# Revit family: Hager-Univers-IP65-D300-H550-Cl.II-encl-CH-fr
name_source: partatom
category: Equipement électrique
units: mm (PartAtom-declared; Revit-internal decimal feet)

## family parameters
Configuration du panneau = Deux colonnes, circuits au sein
Cote de connecteur circulaire = Utiliser le diamètre
Couper avec des vides une fois chargée = Non
Hôte = Face
Partagée = Non
Point de calcul de pièce = Non
Type d'élément = Tableau de raccordement

## types (6) — shared parameters
Commentaires du type = Univers
EF000003 - mode de pose = EV000384 - saillie
EF000007 - couleur = EV000270 - gris
EF000040 - hauteur = 550 mm
EF000049 - profondeur = 300 mm  [stored 0.984252 ft]
EF000116 - numéro RAL = 7035
EF000118 - avec cadre/support de montage = Non
EF000266 - nombre de rangées = 3
EF001088 - possibilité de montage en saillie = Non
EF001131 - profondeur intérieure = 150 mm  [stored 0.492126 ft]
EF001596 - matériau du boîtier/corps = EV000139 - plastique
EF001613 - maintien de fonction = EV000494 - sans
EF003532 - convient pour utilisation à l’extérieur = Oui
EF004293 - indice de protection contre les chocs (IK) = EV008784 - IK10
EF004464 - type de porte = EV002646 - unique
EF005474 - indice de protection (IP) = EV006421 - IP65
EF006244 - couvercle/porte transparent(e) = Non
EF006306 - avec serrure = Oui
EF007800 - adapté à un parafoudre = Oui
EF009170 - épaisseur de matériau du boîtier = 2 mm  [stored 0.00656168 ft]
EF009171 - épaisseur de matériau de la porte/du couvercle = 2 mm  [stored 0.00656168 ft]
EF009212 - finition du couvercle = EV000116 - fermé
EF015940 - couvercle avec décharge de pression = Non
Fabricant = Hager
HG000002 - avec porte = Oui
HG000003 - Gamme = Univers
HG000006 - Encastré = Non
HG000009 - Porte à double battant = Non
HG000010 - Portes asymétriques = Non
HG000023 - Armoire double section = Non
HG000024 - Hauteur de la section basse = 800 mm
HG000026 - Installation au sol = Non
zero-valued in all types: EF000218 - profondeur d'encastrement, EF000437 - nombre d'entrées de conduit, EF009554 - nombre d'ouvertures pour plaques à bride, Elévation par défaut, HG000027 - Hauteur du socle

## per-type parameters (varying)
| type | EF000008 - largeur | EF000339 - type de capot | EF002950 - largeur en nombre de modules | EF004427 - nombre de modules | EF008873 - courant nominal (In) | HG000004 - Référence fabricant |
| saillie IP65 L1100 H550 P300  - FL34S | 1100 mm | EV001012 - couvercle | 48 | 144 | 630 A | FL34S |
| saillie IP65 L1100 H550 P300  - FL34SP | 1100 mm | EV001012 - couvercle | 48 | 144 | 630 A | FL34SP |
| saillie IP65 L600 H550 P300  - FL32S | 600 mm | EV004216 - porte | 24 | 72 | 400 A | FL32S |
| saillie IP65 L600 H550 P300  - FL32SP | 600 mm | EV004216 - porte | 24 | 72 | 400 A | FL32SP |
| saillie IP65 L850 H550 P300  - FL33S | 850 mm  [stored 2.78871 ft] | EV004216 - porte | 36 | 108 | 630 A | FL33S |
| saillie IP65 L850 H550 P300  - FL33SP | 850 mm  [stored 2.78871 ft] | EV004216 - porte | 36 | 108 | 630 A | FL33SP |

note: [stored X ft] marks values corroborated as IEEE doubles in the binary element streams (Revit-internal decimal feet)

## geometry (parser evidence)
native form markers: Sweep x10
no freeform markers — native parametric forms only
